# Revit family: Door-Gate-Panel_ToughGate_CityScapes
name_source: partatom
category: Generic Models
units: mm (PartAtom-declared; Revit-internal decimal feet)

## family parameters
Always vertical = Yes
Can host rebar = No
Cut with Voids When Loaded = No
Part Type = Normal
Room Calculation Point = No
Round Connector Dimension = Use Diameter
Shared = No
Work Plane-Based = No

## types (1)
- Door-Gate-Panel_ToughGate_CityScapes
    CAD Details = https://www.arcat.com
    Default Elevation = 0' - 0"
    Keynote = 32 31 00
    LOUVER SPACING = 9
    Manufacturer = Envisor
    Model = ToughGate
    Panel_Height = 5' - 0"
    Panel_Width = 5' - 0"
    Pole_Left_Viz = 1
    Pole_Right_Viz = 1
    Post_Distance = 0.778839057
    Product Page URL = https://www.arcat.com
    Specification = https://www.arcat.com
    Stiffner_Spacing = 11
    TPole_Height = 5
    URL = https://cityscapesinc.com

## geometry (parser evidence)
native form markers: Sweep x18
no freeform markers — native parametric forms only
